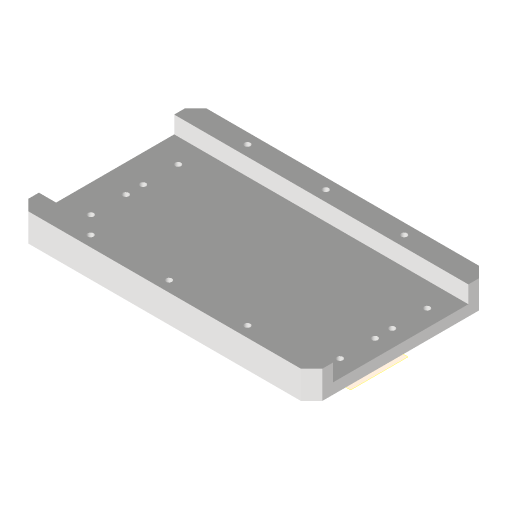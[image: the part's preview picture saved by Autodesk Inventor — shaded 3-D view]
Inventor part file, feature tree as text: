
AUTODESK INVENTOR PART (.ipt)
format: ipt  version: 2024.1 (Build 281209000, 209)  size: 252,416 bytes
history: native  units: mm
features: reference x15, other x5, extrude x3, sketch x3, projected_geometry x2, plane x1, chamfer x1
ambient origin geometry x8: Origin, YZ Plane, XZ Plane, XY Plane, X Axis, Y Axis, Z Axis, Center Point
bodies: Volumenkörper1 (feature_tree)
feature tree (30):
  plane  "Arbeitsebene1"
  extrude  "Extrusion1"  Depth=5.0mm
  chamfer  "Fasen1"  Distance=5.0mm Angle=45.0deg
  extrude  "Extrusion2"  Depth=0.5mm
  extrude  "Extrusion3"  Depth=10.0mm
  sketch  "Skizze1"  dims[d0=5.0mm d1=0.0mm d2=2.8mm d3=5.0mm d4=2.0mm d5=45.0deg]
  reference  "Referenz1"
  reference  "Referenz2"
  reference  "Referenz3"
  reference  "Referenz4"
  reference  "Referenz5"
  reference  "Referenz6"
  reference  "Referenz7"
  reference  "Referenz8"
  reference  "Referenz9"
  reference  "Referenz10"
  reference  "Referenz11"
  reference  "Referenz12"
  sketch  "Skizze2"  dims[d6=0.5mm d7=0.5mm]
  projected_geometry  "Projizierte Kontur1"
  reference  "Referenz13"
  reference  "Referenz14"
  sketch  "Skizze3"  dims[d8=1.0mm d9=0.0mm d10=10.0mm d11=10.0mm d12=8.0mm d13=0.0mm]
  projected_geometry  "Projizierte Kontur2"
  reference  "Referenz15"
  other  "Assembly_Planktoscope_Uc2version_V1.iam"
  other  "60_Planktoscope_Base_half1_MIR:1"
  other  "60_Planktoscope_Base_half1:1"
  other  "60_Planktoscope_Sampleholder:1"
  other  "00_ElectroWallbox_Tpelectric_130x220x140_IP67_Inlet:1"
